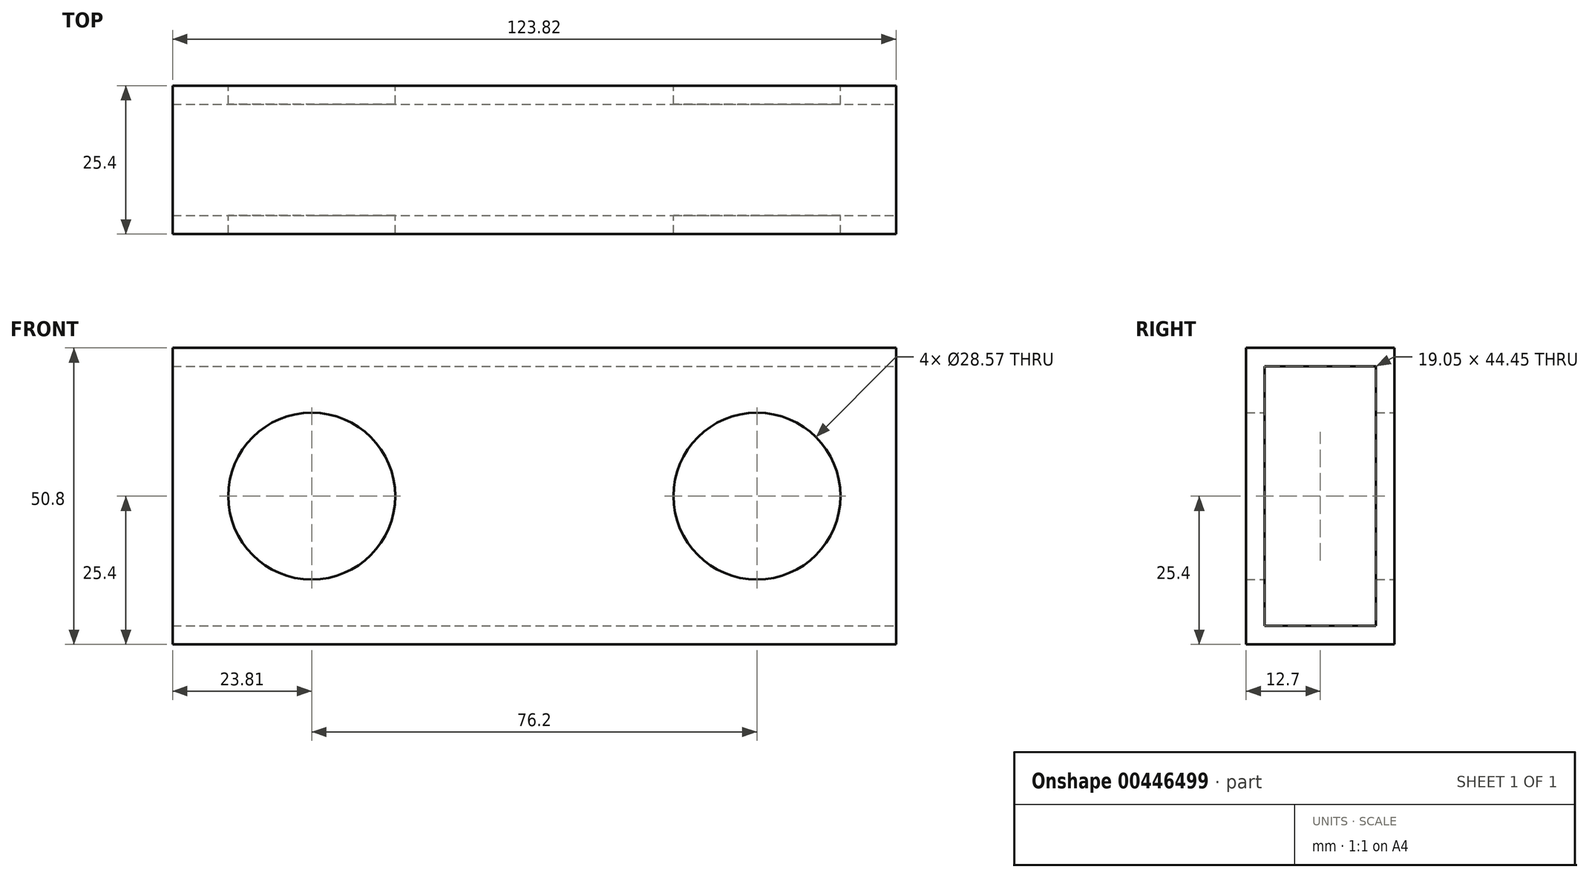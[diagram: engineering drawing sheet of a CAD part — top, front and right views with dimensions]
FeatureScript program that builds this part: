
annotation { "Feature Type Name" : "Feature", "Feature Type Description" : "" }
export const myFeature = defineFeature(function(context is Context, id is Id, definition is map)
    precondition{}
    {
        {
            var Q0;
            Q0=qCreatedBy(makeId("Front.planeOp"),FACE);
            var sketch = newSketch(context, id + "F0", { "sketchPlane" : qUnion([Q0])});
            skLineSegment(sketch, "E0.bottom", {"start": v(61.91, 25.4) * mm, "end": v(-61.91, 25.4) * mm});
            skLineSegment(sketch, "E0.top", {"start": v(61.91, -25.4) * mm, "end": v(-61.91, -25.4) * mm});
            skLineSegment(sketch, "E0.left", {"start": v(61.91, 25.4) * mm, "end": v(61.91, -25.4) * mm});
            skLineSegment(sketch, "E0.right", {"start": v(-61.91, 25.4) * mm, "end": v(-61.91, -25.4) * mm});
            skPoint(sketch, "E0.middle", {"position": v(0, 0) * mm});
            skLineSegment(sketch, "E1", {"start": v(0, 25.4) * mm, "end": v(0, -25.4) * mm, "construction": true});
            skLineSegment(sketch, "E2", {"start": v(0, 0) * mm, "end": v(-61.91, 0) * mm, "construction": true});
            skCircle(sketch, "E3", {"center": v(-38.1, 0) * mm, "radius": 14.29 * mm});
            skCircle(sketch, "E4.MirrorC", {"center": v(38.1, 0) * mm, "radius": 14.29 * mm});
            skSolve(sketch);
        }
        {
            var Q0;
            Q0=makeQuery(id+"F0.imprint","IMPRINT",FACE,{"disambiguationData":[TD([[makeQuery(id+"F0.imprint","IMPRINT",EDGE,{"derivedFrom":sQuery(id+"F0.wireOp",EDGE,"E0.bottom")}),1.0]])]});
            extrude(context, id + "F1", {"entities" : qUnion([Q0]), "depth" : 25.4 * mm, "symmetric" : true});
        }
        {
            var Q0;
            Q0=makeQuery(id+"F1.opExtrude","SWEPT_FACE",FACE,{"disambiguationData":[OSD([sQuery(id+"F0.wireOp",EDGE,"E0.left")])]});
            var sketch = newSketch(context, id + "F2", { "sketchPlane" : qUnion([Q0])});
            skLineSegment(sketch, "E5.0", {"start": v(-9.53, 22.23) * mm, "end": v(9.53, 22.23) * mm});
            skLineSegment(sketch, "E5.1", {"start": v(-9.53, 22.23) * mm, "end": v(-9.53, -22.22) * mm});
            skLineSegment(sketch, "E5.2", {"start": v(-9.53, -22.22) * mm, "end": v(9.53, -22.22) * mm});
            skLineSegment(sketch, "E5.3", {"start": v(9.53, 22.23) * mm, "end": v(9.53, -22.22) * mm});
            skSolve(sketch);
        }
        {
            var Q0;
            Q0=makeQuery(id+"F2.imprint","IMPRINT",FACE,{"disambiguationData":[TD([[makeQuery(id+"F2.imprint","IMPRINT",EDGE,{"derivedFrom":sQuery(id+"F2.wireOp",EDGE,"E5.0")}),-1.0]])]});
            extrude(context, id + "F3", {"entities" : qUnion([Q0]), "operationType" : NewBodyOperationType.REMOVE, "endBound" : BoundingType.THROUGH_ALL, "oppositeDirection" : true, "depth" : 25.4 * mm});
        }
    });
